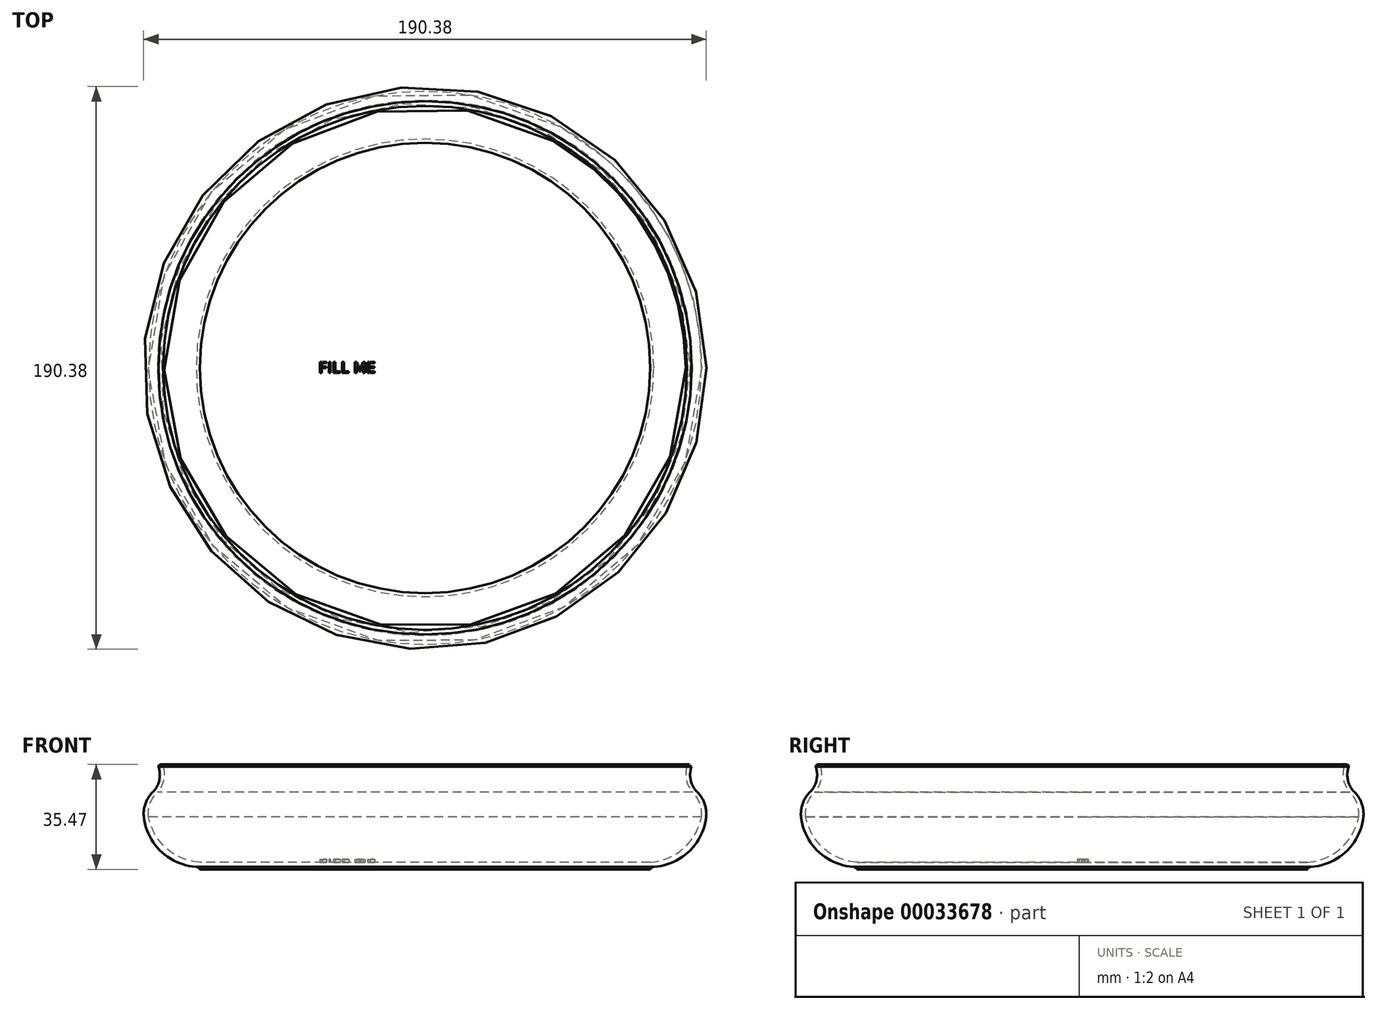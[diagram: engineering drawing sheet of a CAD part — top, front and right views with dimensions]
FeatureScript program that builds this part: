
annotation { "Feature Type Name" : "Feature", "Feature Type Description" : "" }
export const myFeature = defineFeature(function(context is Context, id is Id, definition is map)
    precondition{}
    {
        {
            var Q0;
            Q0=qCreatedBy(makeId("Front.planeOp"),FACE);
            var sketch = newSketch(context, id + "F0", { "sketchPlane" : qUnion([Q0])});
            skLineSegment(sketch, "E0.rect.bottom", {"start": v(-38.1, 0) * mm, "end": v(38.1, 0) * mm});
            skLineSegment(sketch, "E0.rect.top", {"start": v(-38.1, -0.8) * mm, "end": v(38.1, -0.8) * mm});
            skLineSegment(sketch, "E0.rect.left", {"start": v(-38.1, 0) * mm, "end": v(-38.1, -0.8) * mm});
            skLineSegment(sketch, "E0.rect.right", {"start": v(38.1, 0) * mm, "end": v(38.1, -0.8) * mm});
            skPoint(sketch, "E0.rect.middle", {"position": v(0, -0.4) * mm});
            skArc(sketch, "E1", {"start": v(-38.1, 0) * mm, "mid": v(-50.8, 4.85) * mm, "end": v(-57.03, 16.93) * mm});
            skArc(sketch, "E2", {"start": v(-57.03, 16.93) * mm, "mid": v(-56.5, 21.46) * mm, "end": v(-54.05, 25.31) * mm});
            skArc(sketch, "E3", {"start": v(-54.05, 25.31) * mm, "mid": v(-51.8, 29.36) * mm, "end": v(-52.12, 33.99) * mm});
            skPoint(sketch, "E4", {"position": v(-57.03, 16.93) * mm});
            skLineSegment(sketch, "E5", {"start": v(-57.03, 16.93) * mm, "end": v(-55.44, 16.93) * mm});
            skLineSegment(sketch, "E6", {"start": v(-54.05, 25.31) * mm, "end": v(-52.47, 25.31) * mm});
            skArc(sketch, "E7", {"start": v(-52.47, 25.31) * mm, "mid": v(-54.92, 21.46) * mm, "end": v(-55.44, 16.93) * mm});
            skPoint(sketch, "E8", {"position": v(-56.57, 21.28) * mm});
            skPoint(sketch, "E9", {"position": v(-54.98, 21.28) * mm});
            skLineSegment(sketch, "E10", {"start": v(-52.12, 33.99) * mm, "end": v(-50.53, 33.99) * mm});
            skArc(sketch, "E11", {"start": v(-52.47, 25.31) * mm, "mid": v(-50.34, 29.39) * mm, "end": v(-50.53, 33.99) * mm});
            skPoint(sketch, "E12", {"position": v(-51.7, 29.98) * mm});
            skPoint(sketch, "E13", {"position": v(-50.21, 30.06) * mm});
            skLineSegment(sketch, "E14", {"start": v(-38.1, 0) * mm, "end": v(-38.1, 1.59) * mm});
            skArc(sketch, "E15", {"start": v(-55.44, 16.93) * mm, "mid": v(-49.37, 6.32) * mm, "end": v(-38.1, 1.59) * mm});
            skLineSegment(sketch, "E16", {"start": v(-38.1, 1.59) * mm, "end": v(38.1, 1.59) * mm});
            skLineSegment(sketch, "E17", {"start": v(38.1, 1.59) * mm, "end": v(38.1, 0) * mm});
            skArc(sketch, "E18", {"start": v(-50.53, 33.99) * mm, "mid": v(-51.32, 34.68) * mm, "end": v(-52.12, 33.99) * mm});
            skPoint(sketch, "E19", {"position": v(-55.44, 16.93) * mm});
            skPoint(sketch, "E20", {"position": v(1.98, -0.4) * mm});
            skPoint(sketch, "E20.positionSnap0", {"position": v(-38.1, -0.4) * mm});
            skPoint(sketch, "E21", {"position": v(1.98, 0) * mm});
            skPoint(sketch, "E22", {"position": v(33.73, 0.23) * mm});
            skPoint(sketch, "E23", {"position": v(-39.32, 0.04) * mm});
            skArc(sketch, "E24", {"start": v(-38.1, -0.8) * mm, "mid": v(-38.6, -0.22) * mm, "end": v(-39.32, 0.04) * mm});
            skSolve(sketch);
        }
        {
            var Q0;
            Q0 = qSketchRegion(id + "F0", true);
            var Q1;
            Q1=sQuery(id+"F0.wireOp",EDGE,"E17");
            revolve(context, id + "F1", {"entities" : qUnion([Q0]), "axis" : qUnion([Q1]), "revolveType" : RevolveType.FULL});
        }
        {
            var Q0;
            Q0=makeQuery(id+"F1.opRevolve","SWEPT_FACE",FACE,{"disambiguationData":[OSD([sQuery(id+"F0.wireOp",EDGE,"E16")])]});
            var sketch = newSketch(context, id + "F2", { "sketchPlane" : qUnion([Q0])});
            skText(sketch, "E25", { "text": "FILL ME", "fontName": "AllertaStencil-Regular.ttf"});
            const initialGuessF2  = {"E25": [0.00208, -0.00166, 1, 0, 0.00372]};
            skSetInitialGuess(sketch, initialGuessF2);
            skSolve(sketch);
        }
        {
            var Q0;
            Q0 = qSketchRegion(id + "F2", true);
            extrude(context, id + "F3", {"entities" : qUnion([Q0]), "operationType" : NewBodyOperationType.ADD, "depth" : 1.02 * mm});
        }
    });
